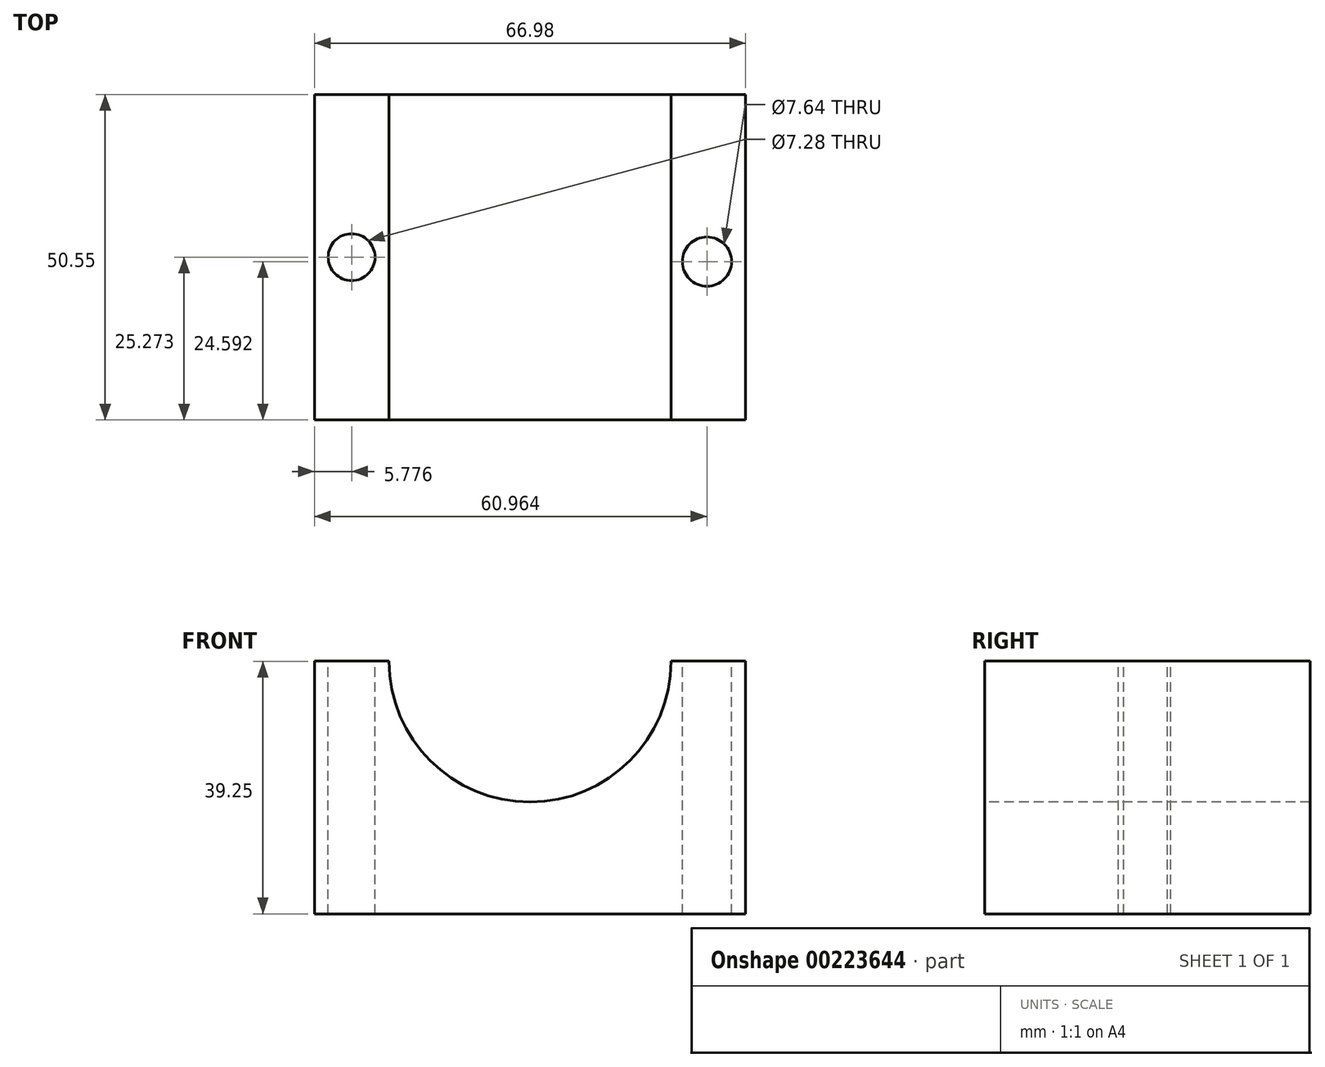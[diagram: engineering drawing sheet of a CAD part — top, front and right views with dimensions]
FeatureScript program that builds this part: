
annotation { "Feature Type Name" : "Feature", "Feature Type Description" : "" }
export const myFeature = defineFeature(function(context is Context, id is Id, definition is map)
    precondition{}
    {
        {
            var Q0;
            Q0=qCreatedBy(makeId("Front.planeOp"),FACE);
            var sketch = newSketch(context, id + "F0", { "sketchPlane" : qUnion([Q0])});
            skLineSegment(sketch, "E0.bottom", {"start": v(-70.2, 50.45) * mm, "end": v(-3.22, 50.45) * mm});
            skLineSegment(sketch, "E0.top", {"start": v(-70.2, 11.2) * mm, "end": v(-3.22, 11.2) * mm});
            skLineSegment(sketch, "E0.left", {"start": v(-70.2, 50.45) * mm, "end": v(-70.2, 11.2) * mm});
            skLineSegment(sketch, "E0.right", {"start": v(-3.22, 50.45) * mm, "end": v(-3.22, 11.2) * mm});
            skSolve(sketch);
        }
        {
            var Q0;
            Q0=makeQuery(id+"F0.imprint","IMPRINT",FACE,{"disambiguationData":[TD([[makeQuery(id+"F0.imprint","IMPRINT",EDGE,{"derivedFrom":sQuery(id+"F0.wireOp",EDGE,"E0.bottom")}),-1.0]])]});
            extrude(context, id + "F1", {"entities" : qUnion([Q0]), "oppositeDirection" : true, "depth" : 50.55 * mm});
        }
        {
            var Q0;
            Q0=makeQuery(id+"F1.opExtrude","CAP_FACE",FACE,{"disambiguationData":[OSD([sQuery(id+"F0.wireOp",EDGE,"E0.bottom"),sQuery(id+"F0.wireOp",EDGE,"E0.top"),sQuery(id+"F0.wireOp",EDGE,"E0.left"),sQuery(id+"F0.wireOp",EDGE,"E0.right")])],"isStart":true});
            var sketch = newSketch(context, id + "F2", { "sketchPlane" : qUnion([Q0])});
            skCircle(sketch, "E1", {"center": v(-36.71, 50.45) * mm, "radius": 21.89 * mm});
            skSolve(sketch);
        }
        {
            var Q0;
            {var subQ0=sQuery(id+"F2.wireOp",EDGE,"E1");var subQ1=makeQuery(id+"F1.opExtrude","CAP_EDGE",EDGE,{"disambiguationData":[OSD([sQuery(id+"F0.wireOp",EDGE,"E0.bottom")])],"isStart":true});var subQ2=makeQuery(id+"F2.imprint","INTERSECT",VERTEX,{"disambiguationData":[OD(0.0)],"derivedFrom":[subQ1,subQ0]});Q0=makeQuery(id+"F2.imprint","IMPRINT",FACE,{"disambiguationData":[TD([[makeQuery(id+"F2.imprint","IMPRINT",EDGE,{"disambiguationData":[TD([[subQ2,-1.0]])],"derivedFrom":subQ0}),1.0]])]});}
            var Q1;
            {var subQ0=sQuery(id+"F2.wireOp",EDGE,"E1");var subQ1=makeQuery(id+"F1.opExtrude","CAP_EDGE",EDGE,{"disambiguationData":[OSD([sQuery(id+"F0.wireOp",EDGE,"E0.bottom")])],"isStart":true});var subQ2=makeQuery(id+"F2.imprint","INTERSECT",VERTEX,{"disambiguationData":[OD(0.0)],"derivedFrom":[subQ1,subQ0]});Q1=makeQuery(id+"F2.imprint","IMPRINT",FACE,{"disambiguationData":[TD([[makeQuery(id+"F2.imprint","IMPRINT",EDGE,{"disambiguationData":[TD([[subQ2,1.0]])],"derivedFrom":subQ0}),1.0]])]});}
            extrude(context, id + "F3", {"entities" : qUnion([Q0, Q1]), "operationType" : NewBodyOperationType.REMOVE, "oppositeDirection" : true, "depth" : 60.2 * mm});
        }
        {
            var Q0;
            {var subQ1=sQuery(id+"F0.wireOp",EDGE,"E0.left");var subQ3=sQuery(id+"F0.wireOp",EDGE,"E0.bottom");Q0=makeQuery(id+"F3.boolean.opBoolean","SPLIT",FACE,{"disambiguationData":[TD([makeQuery(id+"F1.opExtrude","SWEPT_FACE",FACE,{"disambiguationData":[OSD([subQ1])]})])],"derivedFrom":makeQuery(id+"F1.opExtrude","SWEPT_FACE",FACE,{"disambiguationData":[OSD([subQ3])]})});}
            var sketch = newSketch(context, id + "F4", { "sketchPlane" : qUnion([Q0])});
            skCircle(sketch, "E2", {"center": v(-64.42, 25.27) * mm, "radius": 3.64 * mm});
            skPoint(sketch, "E2.centerSnap0", {"position": v(-70.2, 25.27) * mm});
            skCircle(sketch, "E3", {"center": v(-9.24, 24.6) * mm, "radius": 3.82 * mm});
            skSolve(sketch);
        }
        {
            var Q0;
            Q0=makeQuery(id+"F4.imprint","IMPRINT",FACE,{"disambiguationData":[TD([[makeQuery(id+"F4.imprint","IMPRINT",EDGE,{"derivedFrom":sQuery(id+"F4.wireOp",EDGE,"E2")}),1.0]])]});
            var Q1;
            Q1=makeQuery(id+"F4.imprint","IMPRINT",FACE,{"disambiguationData":[TD([[makeQuery(id+"F4.imprint","IMPRINT",EDGE,{"derivedFrom":sQuery(id+"F4.wireOp",EDGE,"E3")}),1.0]])]});
            extrude(context, id + "F5", {"entities" : qUnion([Q0, Q1]), "operationType" : NewBodyOperationType.REMOVE, "oppositeDirection" : true, "depth" : 136.65 * mm});
        }
    });
